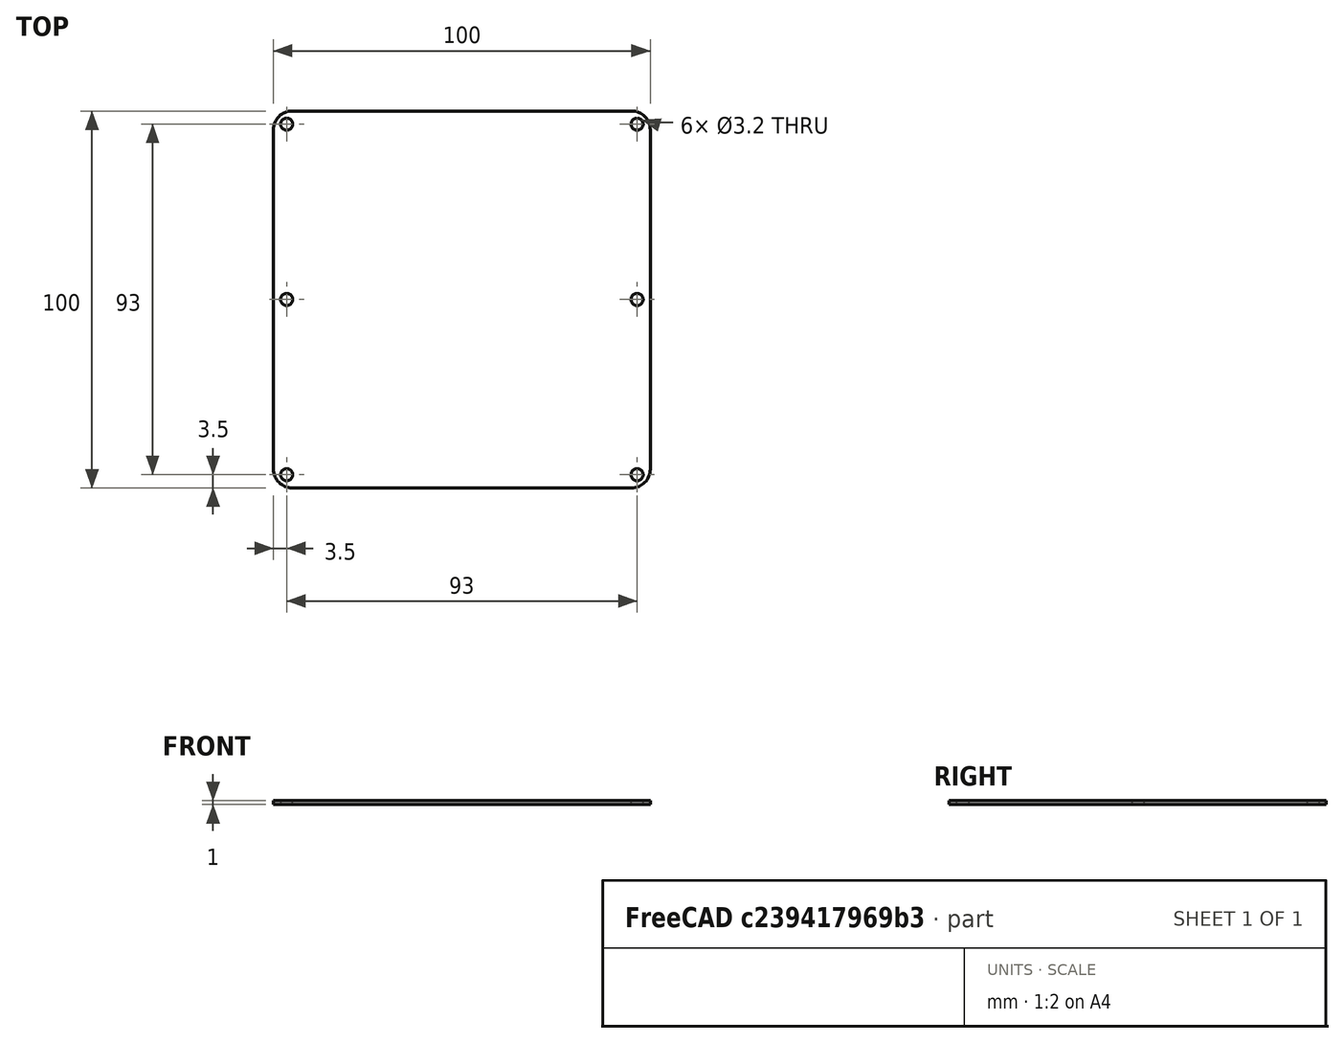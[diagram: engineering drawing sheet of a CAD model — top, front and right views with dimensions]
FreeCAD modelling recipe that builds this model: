
FCSTD DOCUMENT  (FreeCAD 0.20R29177 +426 (Git))
Label: UINIO-Board-Edge
License: All rights reserved
LicenseURL: http://en.wikipedia.org/wiki/All_rights_reserved
objects: Sketcher::SketchObject×1, PartDesign::Pad×1, PartDesign::Body×1
note: 4 computed .brp shape members not serialized (recipe doc carries the construction recipe); baked Part::Feature solids carry a one-line shape summary decoded from their .brp

FEATURE [Sketcher::SketchObject] Sketch
  FullyConstrained = false
  MapMode = 5
  Support = -> [XY_Plane]
  sketch-geometry (18):
    g0: LineSegment StartX=-45 StartY=50 StartZ=0 EndX=45 EndY=50 EndZ=0
    g1: LineSegment StartX=50 StartY=45 StartZ=0 EndX=50 EndY=-45 EndZ=0
    g2: LineSegment StartX=45 StartY=-50 StartZ=0 EndX=-45 EndY=-50 EndZ=0
    g3: LineSegment StartX=-50 StartY=-45 StartZ=0 EndX=-50 EndY=45 EndZ=0
    g4: ArcOfCircle CenterX=45 CenterY=45 CenterZ=0 NormalX=0 NormalY=0 NormalZ=1 AngleXU=0 Radius=5 StartAngle=4e-16 EndAngle=1.5708
    g5: ArcOfCircle CenterX=45 CenterY=-45 CenterZ=0 NormalX=0 NormalY=0 NormalZ=1 AngleXU=0 Radius=5 StartAngle=4.71239 EndAngle=6.28319
    g6: ArcOfCircle CenterX=-45 CenterY=-45 CenterZ=0 NormalX=0 NormalY=0 NormalZ=1 AngleXU=0 Radius=5 StartAngle=3.14159 EndAngle=4.71239
    g7: ArcOfCircle CenterX=-45 CenterY=45 CenterZ=0 NormalX=0 NormalY=0 NormalZ=1 AngleXU=0 Radius=5 StartAngle=1.5708 EndAngle=3.14159
    g8: Circle CenterX=-46.5 CenterY=46 CenterZ=0 NormalX=0 NormalY=0 NormalZ=1 AngleXU=0 Radius=1.6
    g9: GeomPoint X=112.589 Y=63.8453 Z=0
    g10: GeomPoint X=117.799 Y=28.0513 Z=0
    g11: GeomPoint X=116.573 Y=-3.45234 Z=0
    g12: GeomPoint X=114.735 Y=24.1286 Z=0
    g13: Circle CenterX=-46.5 CenterY=-46 CenterZ=0 NormalX=0 NormalY=0 NormalZ=1 AngleXU=0 Radius=1.6
    g14: Circle CenterX=-46.5 CenterY=0 CenterZ=0 NormalX=0 NormalY=0 NormalZ=1 AngleXU=0 Radius=1.6
    g15: Circle CenterX=46.5 CenterY=0 CenterZ=0 NormalX=0 NormalY=0 NormalZ=1 AngleXU=0 Radius=1.6
    g16: Circle CenterX=46.5 CenterY=46 CenterZ=0 NormalX=0 NormalY=0 NormalZ=1 AngleXU=0 Radius=1.6
    g17: Circle CenterX=46.5 CenterY=-46 CenterZ=0 NormalX=0 NormalY=0 NormalZ=1 AngleXU=0 Radius=1.6
  constraints (37):
    c: Horizontal(g0)
    c: Horizontal(g2)
    c: Vertical(g1)
    c: Vertical(g3)
    c: Tangent(g0,g4) = 1.5708
    c: Tangent(g1,g4) = 1.5708
    c: Tangent(g2,g5) = 1.5708
    c: Tangent(g1,g5) = 1.5708
    c: Tangent(g3,g6) = 1.5708
    c: Tangent(g2,g6) = 1.5708
    c: Tangent(g0,g7) = 1.5708
    c: Tangent(g3,g7) = 1.5708
    c: Radius(g7) = 5
    c: Radius(g4) = 5
    c: Radius(g5) = 5
    c: Radius(g6) = 5
    c: Distance(g3,g1) = 100
    c: Distance(g2,g0) = 100
    c: Symmetric(g7,g5,g-1)
    c: Diameter(g8) = 3.2
    c: Diameter(g13) = 3.2
    c: Diameter(g15) = 3.2
    c: Diameter(g16) = 3.2
    c: Diameter(g17) = 3.2
    c: Diameter(g14) = 3.2
    c: PointOnObject(g14,g-1)
    c: PointOnObject(g15,g-1)
    c: Distance(g14,g3) = 3.5
    c: Distance(g8,g3) = 3.5
    c: Distance(g8,g0) = 4
    c: Distance(g13,g3) = 3.5
    c: Distance(g13,g2) = 4
    c: Distance(g16,g0) = 4
    c: Distance(g16,g1) = 3.5
    c: Distance(g15,g1) = 3.5
    c: Distance(g17,g1) = 3.5
    c: Distance(g17,g2) = 4
FEATURE [PartDesign::Pad] Pad
  Direction = (0,0,1)
  Length = 1
  Length2 = 10
  Profile = -> Sketch
  ReferenceAxis = -> Sketch [N_Axis]
  Type = 0
FEATURE [PartDesign::Body] Body
  Group = -> [Sketch,Pad]
  Origin = -> Origin
  Tip = -> Pad
